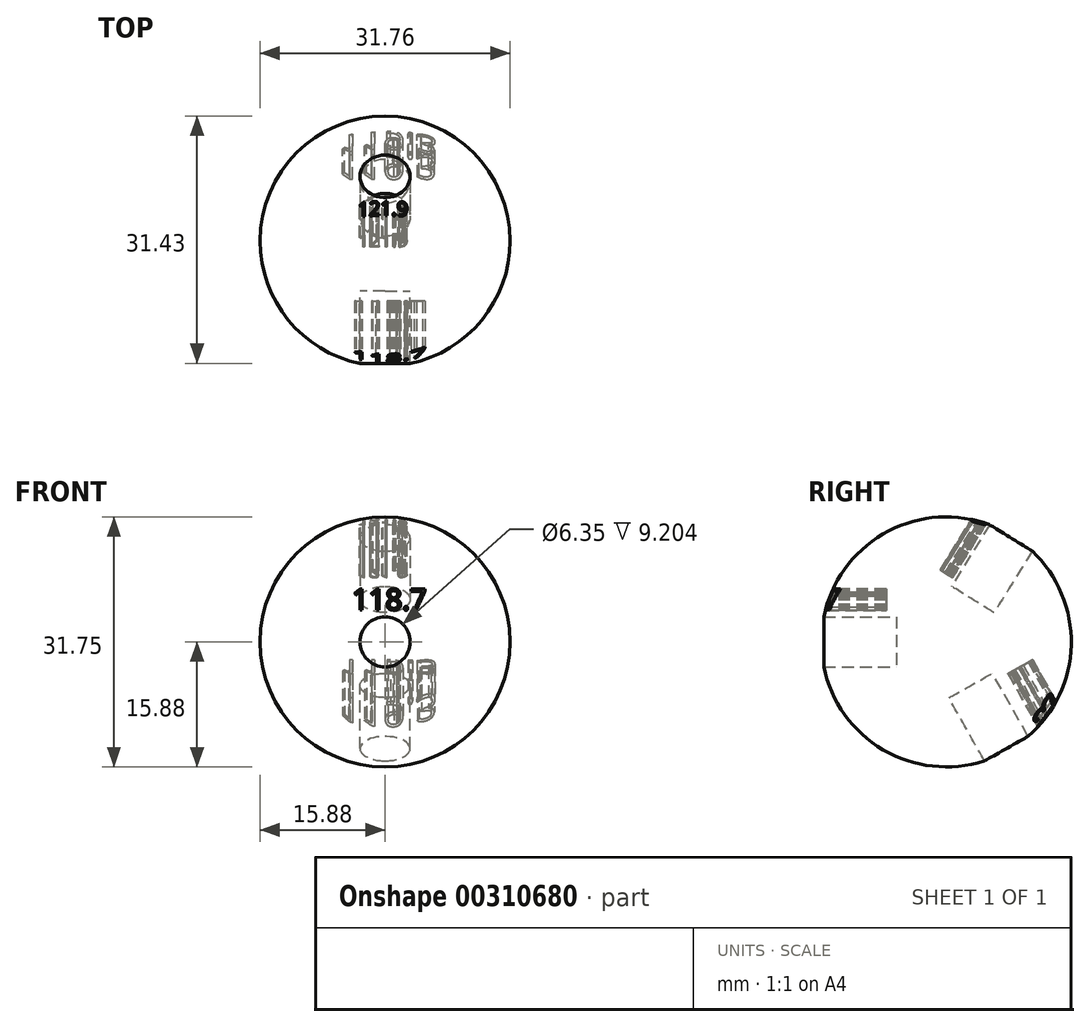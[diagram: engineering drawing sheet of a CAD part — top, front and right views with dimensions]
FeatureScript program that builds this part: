
annotation { "Feature Type Name" : "Feature", "Feature Type Description" : "" }
export const myFeature = defineFeature(function(context is Context, id is Id, definition is map)
    precondition{}
    {
        {
            var Q0;
            Q0=qCreatedBy(makeId("Front.planeOp"),FACE);
            var sketch = newSketch(context, id + "F0", { "sketchPlane" : qUnion([Q0])});
            skArc(sketch, "E0", {"start": v(-15.88, 0) * mm, "mid": v(0, -15.88) * mm, "end": v(15.88, 0) * mm});
            skLineSegment(sketch, "E1", {"start": v(1.66, 0) * mm, "end": v(15.88, 0) * mm});
            skLineSegment(sketch, "E2", {"start": v(1.66, 0) * mm, "end": v(-15.88, 0) * mm});
            skSolve(sketch);
        }
        {
            var Q0;
            Q0=qCreatedBy(makeId("Right.planeOp"),FACE);
            var sketch = newSketch(context, id + "F1", { "sketchPlane" : qUnion([Q0])});
            skCircle(sketch, "E3", {"center": v(0, 0) * mm, "radius": 15.88 * mm});
            skSolve(sketch);
        }
        {
            var Q0;
            Q0 = qSketchRegion(id + "F0", true);
            var Q1;
            Q1=sQuery(id+"F1.wireOp",EDGE,"E3");
            revolve(context, id + "F2", {"entities" : qUnion([Q0]), "axis" : qUnion([Q1]), "revolveType" : RevolveType.FULL});
        }
        {
            var Q0;
            Q0=qCreatedBy(makeId("Front.planeOp"),FACE);
            cPlane(context, id + "F3", {"entities" : qUnion([Q0]), "cplaneType" : CPlaneType.OFFSET, "offset" : 6.35 * mm, "width" : 152.4 * mm, "height" : 152.4 * mm});
        }
        {
            var Q0;
            Q0=qCreatedBy(id+"F3.planeOp",FACE);
            var sketch = newSketch(context, id + "F4", { "sketchPlane" : qUnion([Q0])});
            skCircle(sketch, "E4", {"center": v(0, 0) * mm, "radius": 3.18 * mm});
            skSolve(sketch);
        }
        {
            var Q0;
            Q0 = qSketchRegion(id + "F4", true);
            extrude(context, id + "F5", {"entities" : qUnion([Q0]), "depth" : 25.4 * mm});
        }
        {
            var Q0;
            Q0=qCreatedBy(makeId("Top.planeOp"),FACE);
            var sketch = newSketch(context, id + "F6", { "sketchPlane" : qUnion([Q0])});
            skLineSegment(sketch, "E5", {"start": v(-61.4, 0) * mm, "end": v(72.27, 0) * mm, "construction": true});
            skSolve(sketch);
        }
        {
            var Q0;
            Q0=makeQuery(id+"F5.opExtrude","SWEPT_BODY",BODY,{"disambiguationData":[OSD([sQuery(id+"F4.wireOp",EDGE,"E4")])]});
            var Q1;
            Q1=sQuery(id+"F6.wireOp",EDGE,"E5");
            transform(context, id + "F7", {"entities" : qUnion([Q0]), "transformType" : TransformType.ROTATION, "transformAxis" : qUnion([Q1]), "angle" : 119.3 * degree, "makeCopy" : true});
        }
        {
            var Q0;
            Q0=qCreatedBy(makeId("Top.planeOp"),FACE);
            var sketch = newSketch(context, id + "F8", { "sketchPlane" : qUnion([Q0])});
            skLineSegment(sketch, "E6", {"start": v(-74.11, 0) * mm, "end": v(68.58, 0) * mm, "construction": true});
            skSolve(sketch);
        }
        {
            var Q0;
            Q0=makeQuery(id+"F5.opExtrude","SWEPT_BODY",BODY,{"disambiguationData":[OSD([sQuery(id+"F4.wireOp",EDGE,"E4")])]});
            var Q1;
            Q1=sQuery(id+"F8.wireOp",EDGE,"E6");
            transform(context, id + "F9", {"entities" : qUnion([Q0]), "transformType" : TransformType.ROTATION, "transformAxis" : qUnion([Q1]), "angle" : 121.9 * degree, "oppositeDirection" : true, "makeCopy" : true});
        }
        {
            var Q0;
            Q0=qCreatedBy(id+"F3.planeOp",FACE);
            cPlane(context, id + "F10", {"entities" : qUnion([Q0]), "cplaneType" : CPlaneType.OFFSET, "offset" : 11.43 * mm, "width" : 152.4 * mm, "height" : 152.4 * mm});
        }
        {
            var Q0;
            Q0=qCreatedBy(id+"F10.planeOp",FACE);
            var sketch = newSketch(context, id + "F11", { "sketchPlane" : qUnion([Q0])});
            skText(sketch, "E7", { "text": "118.7", "fontName": "OpenSans-Regular.ttf"});
            const initialGuessF11  = {"E7": [-0.00419, 0.00406, 1, 0, 0.00267]};
            skSetInitialGuess(sketch, initialGuessF11);
            skSolve(sketch);
        }
        {
            var Q0;
            Q0 = qSketchRegion(id + "F11", true);
            extrude(context, id + "F12", {"entities" : qUnion([Q0]), "operationType" : NewBodyOperationType.REMOVE, "oppositeDirection" : true, "depth" : 10.16 * mm});
        }
        {
            var Q0;
            Q0=makeQuery(id+"F9.opPattern","COPY",FACE,{"derivedFrom":makeQuery(id+"F5.opExtrude","CAP_FACE",FACE,{"disambiguationData":[OSD([sQuery(id+"F4.wireOp",EDGE,"E4")])],"isStart":false}),"instanceName":"1"});
            cPlane(context, id + "F13", {"entities" : qUnion([Q0]), "cplaneType" : CPlaneType.OFFSET, "offset" : 14.22 * mm, "oppositeDirection" : true, "width" : 152.4 * mm, "height" : 152.4 * mm});
        }
        {
            var Q0;
            Q0=qCreatedBy(id+"F13.planeOp",FACE);
            var sketch = newSketch(context, id + "F14", { "sketchPlane" : qUnion([Q0])});
            skText(sketch, "E8", { "text": "121.9", "fontName": "OpenSans-Regular.ttf"});
            const initialGuessF14  = {"E8": [-0.00346, -0.00545, 1, 0, 0.0018]};
            skSetInitialGuess(sketch, initialGuessF14);
            skSolve(sketch);
        }
        {
            var Q0;
            Q0 = qSketchRegion(id + "F14", true);
            extrude(context, id + "F15", {"entities" : qUnion([Q0]), "operationType" : NewBodyOperationType.REMOVE, "oppositeDirection" : true, "depth" : 10.16 * mm});
        }
        {
            var Q0;
            Q0=makeQuery(id+"F7.opPattern","COPY",FACE,{"derivedFrom":makeQuery(id+"F5.opExtrude","CAP_FACE",FACE,{"disambiguationData":[OSD([sQuery(id+"F4.wireOp",EDGE,"E4")])],"isStart":false}),"instanceName":"1"});
            cPlane(context, id + "F16", {"entities" : qUnion([Q0]), "cplaneType" : CPlaneType.OFFSET, "offset" : 14.22 * mm, "oppositeDirection" : true, "width" : 152.4 * mm, "height" : 152.4 * mm});
        }
        {
            var Q0;
            Q0=qCreatedBy(id+"F16.planeOp",FACE);
            var sketch = newSketch(context, id + "F17", { "sketchPlane" : qUnion([Q0])});
            skText(sketch, "E9", { "text": "119.3", "fontName": "OpenSans-Regular.ttf"});
            const initialGuessF17  = {"E9": [-0.00583, -0.00838, 1, 0, 0.00352]};
            skSetInitialGuess(sketch, initialGuessF17);
            skSolve(sketch);
        }
        {
            var Q0;
            Q0 = qSketchRegion(id + "F17", true);
            extrude(context, id + "F18", {"entities" : qUnion([Q0]), "operationType" : NewBodyOperationType.REMOVE, "oppositeDirection" : true, "depth" : 10.16 * mm});
        }
        {
            var Q0;
            Q0=makeQuery(id+"F5.opExtrude","SWEPT_BODY",BODY,{"disambiguationData":[OSD([sQuery(id+"F4.wireOp",EDGE,"E4")])]});
            var Q1;
            Q1=makeQuery(id+"F9.opPattern","COPY",BODY,{"derivedFrom":makeQuery(id+"F5.opExtrude","SWEPT_BODY",BODY,{"disambiguationData":[OSD([sQuery(id+"F4.wireOp",EDGE,"E4")])]}),"instanceName":"1"});
            var Q2;
            Q2=makeQuery(id+"F7.opPattern","COPY",BODY,{"derivedFrom":makeQuery(id+"F5.opExtrude","SWEPT_BODY",BODY,{"disambiguationData":[OSD([sQuery(id+"F4.wireOp",EDGE,"E4")])]}),"instanceName":"1"});
            var Q3;
            Q3=makeQuery(id+"F2.opRevolve","SWEPT_BODY",BODY,{"disambiguationData":[OSD([sQuery(id+"F0.wireOp",EDGE,"E0"),sQuery(id+"F0.wireOp",EDGE,"E1"),sQuery(id+"F0.wireOp",EDGE,"E2")])]});
            booleanBodies(context, id + "F19", {"operationType" : BooleanOperationType.SUBTRACTION, "tools" : qUnion([Q0, Q1, Q2]), "targets" : qUnion([Q3])});
        }
    });
